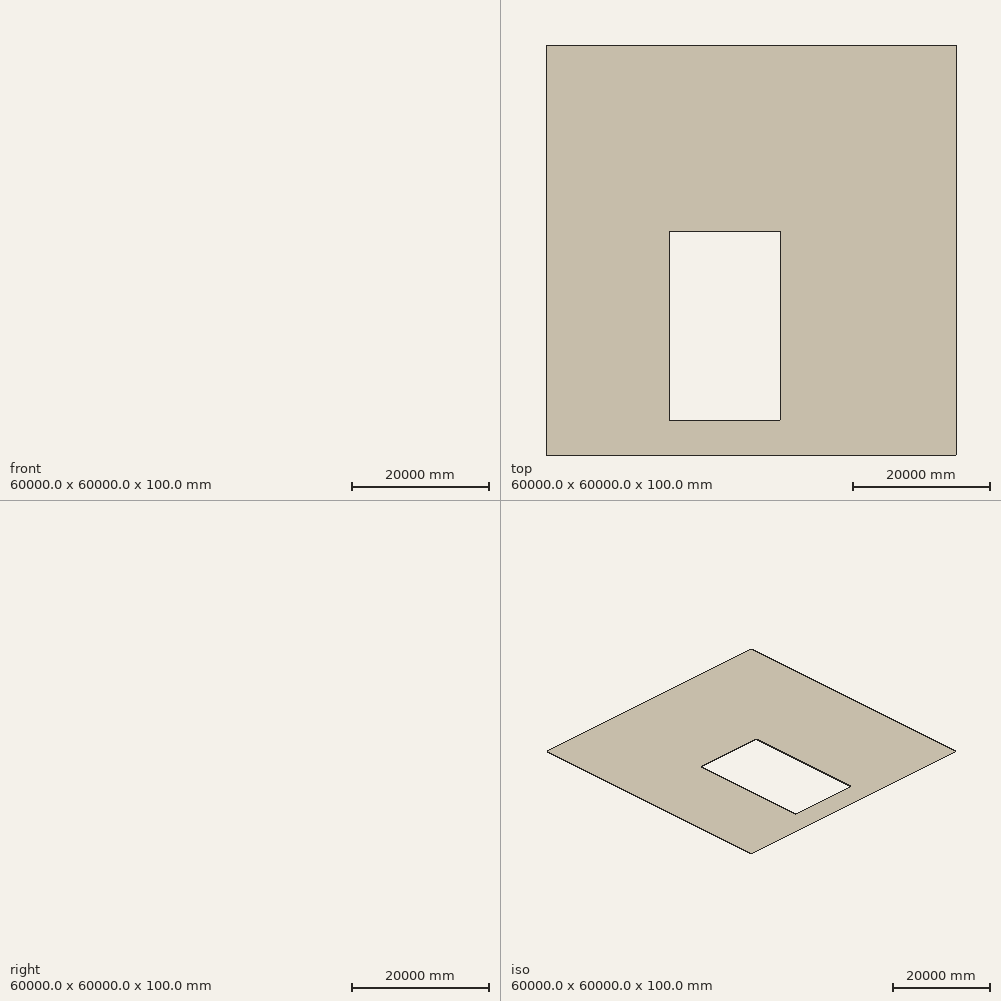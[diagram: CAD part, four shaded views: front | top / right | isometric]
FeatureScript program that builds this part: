
annotation { "Feature Type Name" : "Feature", "Feature Type Description" : "" }
export const myFeature = defineFeature(function(context is Context, id is Id, definition is map)
    precondition{}
    {
        {
            var Q0;
            Q0=qCreatedBy(makeId("Top.planeOp"),FACE);
            var sketch = newSketch(context, id + "F0", { "sketchPlane" : qUnion([Q0])});
            skLineSegment(sketch, "E0.bottom", {"start": v(0, 0) * mm, "end": v(60000, 0) * mm});
            skLineSegment(sketch, "E0.top", {"start": v(0, -60000) * mm, "end": v(60000, -60000) * mm});
            skLineSegment(sketch, "E0.left", {"start": v(0, 0) * mm, "end": v(0, -60000) * mm});
            skLineSegment(sketch, "E0.right", {"start": v(60000, 0) * mm, "end": v(60000, -60000) * mm});
            skLineSegment(sketch, "E1.bottom", {"start": v(24000, -30000) * mm, "end": v(28000, -30000) * mm});
            skLineSegment(sketch, "E1.top", {"start": v(24000, -36000) * mm, "end": v(28000, -36000) * mm});
            skLineSegment(sketch, "E1.left", {"start": v(24000, -30000) * mm, "end": v(24000, -36000) * mm});
            skLineSegment(sketch, "E1.right", {"start": v(28000, -30000) * mm, "end": v(28000, -36000) * mm});
            skLineSegment(sketch, "E2.bottom", {"start": v(18036.38, -27194.53) * mm, "end": v(34311.55, -27194.53) * mm});
            skLineSegment(sketch, "E2.top", {"start": v(18036.38, -54872.59) * mm, "end": v(34311.55, -54872.59) * mm});
            skLineSegment(sketch, "E2.left", {"start": v(18036.38, -27194.53) * mm, "end": v(18036.38, -54872.59) * mm});
            skLineSegment(sketch, "E2.right", {"start": v(34311.55, -27194.53) * mm, "end": v(34311.55, -54872.59) * mm});
            skLineSegment(sketch, "E3.bottom", {"start": v(33907.18, -54872.59) * mm, "end": v(34311.55, -54872.59) * mm});
            skLineSegment(sketch, "E3.top", {"start": v(33907.18, -38721.86) * mm, "end": v(34311.55, -38721.86) * mm});
            skLineSegment(sketch, "E3.left", {"start": v(34311.55, -54872.59) * mm, "end": v(34311.55, -38721.86) * mm});
            skLineSegment(sketch, "E3.right", {"start": v(33907.18, -54872.59) * mm, "end": v(33907.18, -38721.86) * mm});
            skSolve(sketch);
        }
        {
            var Q0;
            Q0 = qSketchRegion(id + "F0", true);
            var Q1;
            Q1=makeQuery(id+"F0.imprint","IMPRINT",FACE,{"disambiguationData":[TD([[makeQuery(id+"F0.imprint","IMPRINT",EDGE,{"derivedFrom":sQuery(id+"F0.wireOp",EDGE,"E3.bottom")}),1.0]])]});
            extrude(context, id + "F1", {"entities" : qUnion([Q0, Q1]), "depth" : 100 * mm, "offsetDistance" : 25 * mm});
        }
    });
